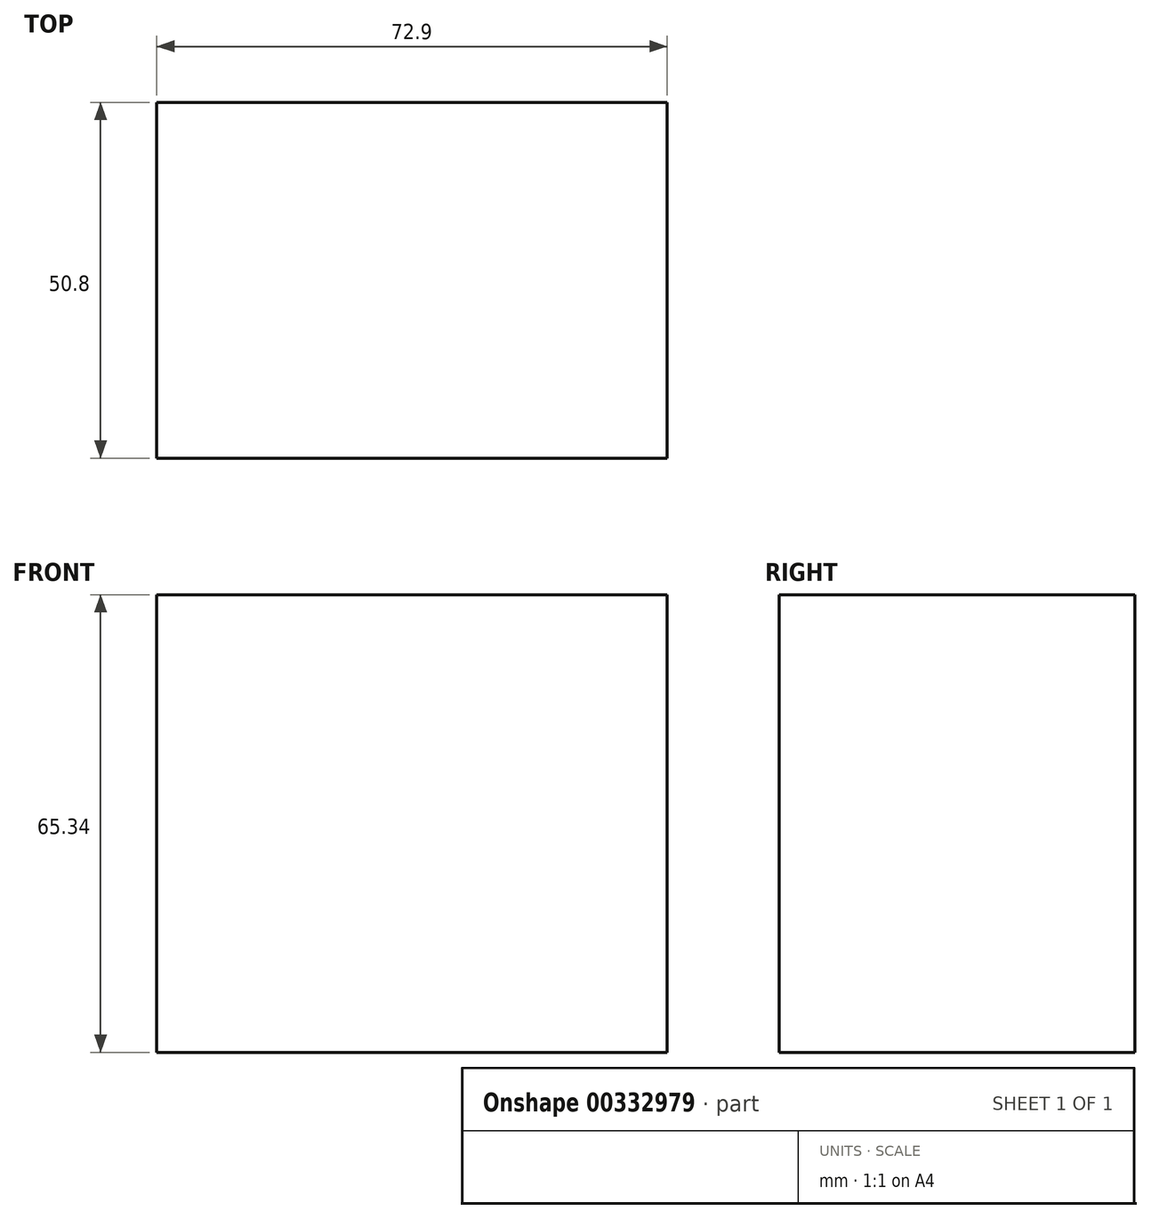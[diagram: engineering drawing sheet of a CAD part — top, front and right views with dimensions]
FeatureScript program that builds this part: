
annotation { "Feature Type Name" : "Feature", "Feature Type Description" : "" }
export const myFeature = defineFeature(function(context is Context, id is Id, definition is map)
    precondition{}
    {
        {
            var Q0;
            Q0=qCreatedBy(makeId("Front.planeOp"),FACE);
            var sketch = newSketch(context, id + "F0", { "sketchPlane" : qUnion([Q0])});
            skLineSegment(sketch, "E0.bottom", {"start": v(-62.23, 25.56) * mm, "end": v(10.67, 25.56) * mm});
            skLineSegment(sketch, "E0.top", {"start": v(-62.23, -39.78) * mm, "end": v(10.67, -39.78) * mm});
            skLineSegment(sketch, "E0.left", {"start": v(-62.23, 25.56) * mm, "end": v(-62.23, -39.78) * mm});
            skLineSegment(sketch, "E0.right", {"start": v(10.67, 25.56) * mm, "end": v(10.67, -39.78) * mm});
            skSolve(sketch);
        }
        {
            var Q0;
            Q0=makeQuery(id+"F0.imprint","IMPRINT",FACE,{"disambiguationData":[TD([[makeQuery(id+"F0.imprint","IMPRINT",EDGE,{"derivedFrom":sQuery(id+"F0.wireOp",EDGE,"E0.bottom")}),-1.0]])]});
            extrude(context, id + "F1", {"entities" : qUnion([Q0]), "depth" : 50.8 * mm});
        }
    });
